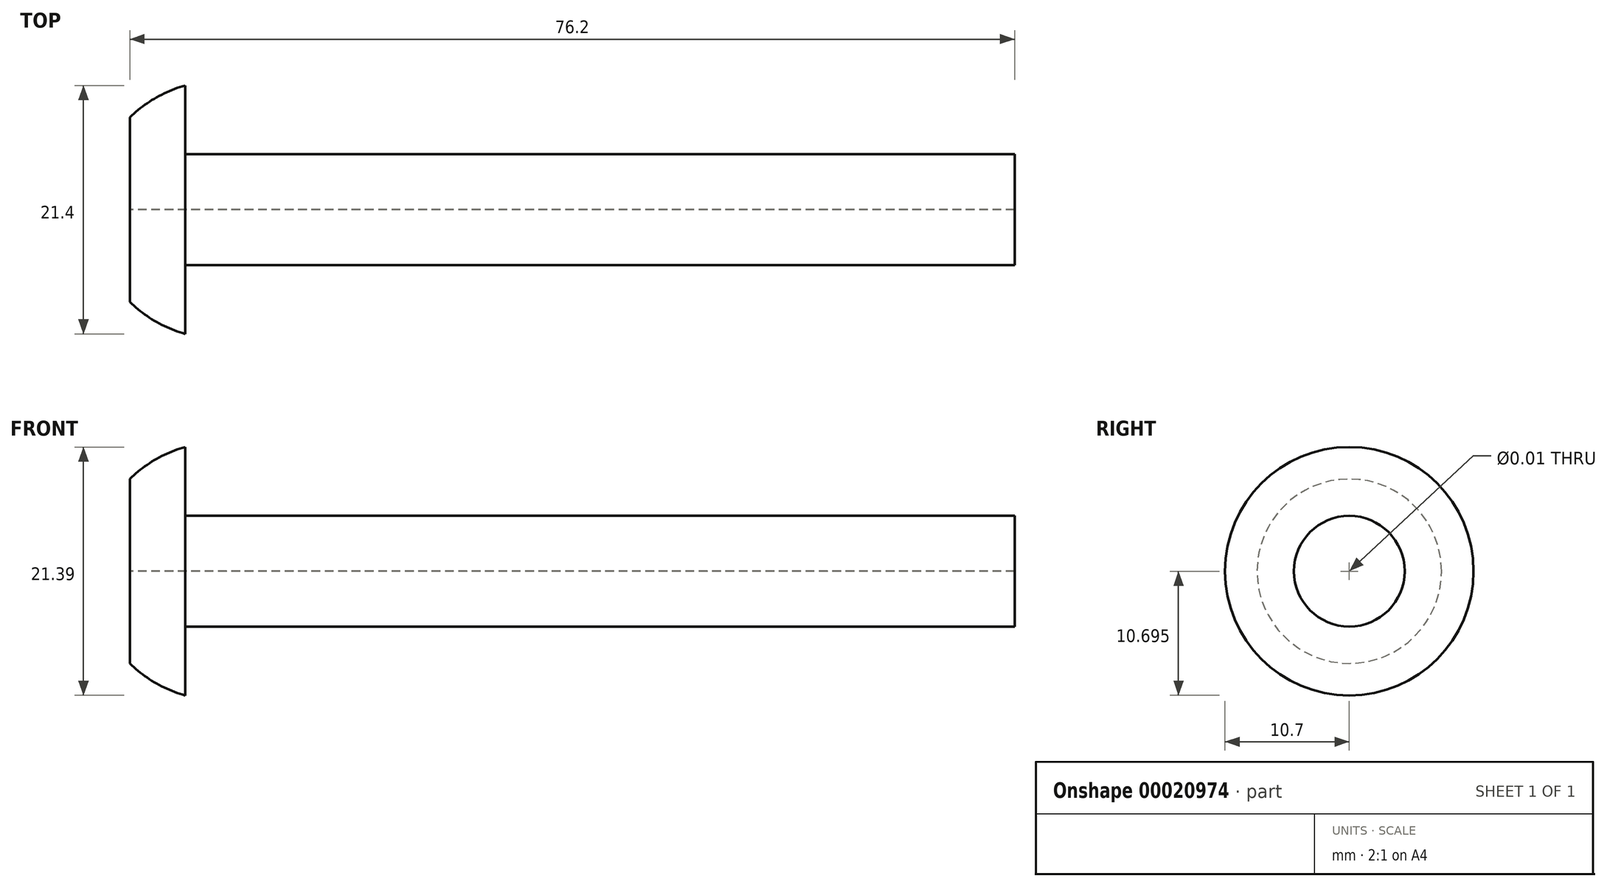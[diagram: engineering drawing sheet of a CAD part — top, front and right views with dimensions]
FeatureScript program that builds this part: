
annotation { "Feature Type Name" : "Feature", "Feature Type Description" : "" }
export const myFeature = defineFeature(function(context is Context, id is Id, definition is map)
    precondition{}
    {
        {
            var Q0;
            Q0=qCreatedBy(makeId("Front.planeOp"),FACE);
            var sketch = newSketch(context, id + "F0", { "sketchPlane" : qUnion([Q0])});
            skPoint(sketch, "E0", {"position": v(31.69, -5.39) * mm});
            skLineSegment(sketch, "E1", {"start": v(40.38, 12.9) * mm, "end": v(40.38, 4.95) * mm});
            skLineSegment(sketch, "E2", {"start": v(40.38, 12.9) * mm, "end": v(43.55, 12.9) * mm});
            skLineSegment(sketch, "E3", {"start": v(43.55, 12.9) * mm, "end": v(45.14, 12.9) * mm});
            skLineSegment(sketch, "E4", {"start": v(43.55, 12.9) * mm, "end": v(43.55, 2.78) * mm});
            skLineSegment(sketch, "E5", {"start": v(45.14, 2.2) * mm, "end": v(45.14, 12.9) * mm});
            skArc(sketch, "E6.trimOffspring", {"start": v(40.38, 4.95) * mm, "mid": v(42.58, 3.28) * mm, "end": v(45.14, 2.2) * mm});
            skLineSegment(sketch, "E7", {"start": v(45.14, 12.9) * mm, "end": v(116.58, 12.9) * mm});
            skLineSegment(sketch, "E8", {"start": v(116.58, 12.9) * mm, "end": v(116.58, 8.13) * mm});
            skLineSegment(sketch, "E9", {"start": v(116.58, 8.13) * mm, "end": v(45.14, 8.13) * mm});
            skPoint(sketch, "E10.orphan", {"position": v(43.55, 23) * mm});
            skPoint(sketch, "E11.orphan", {"position": v(40.38, 20.83) * mm});
            skPoint(sketch, "E12.end.orphan", {"position": v(36.45, -10.16) * mm});
            skPoint(sketch, "E13.end.orphan", {"position": v(36.45, -14.92) * mm});
            skPoint(sketch, "E13.start.orphan", {"position": v(34.86, -14.92) * mm});
            skPoint(sketch, "E14.orphan", {"position": v(31.69, -5.4) * mm});
            skPoint(sketch, "E15.end.orphan", {"position": v(36.45, -5.4) * mm});
            skLineSegment(sketch, "E16", {"start": v(40.38, 12.9) * mm, "end": v(116.58, 12.9) * mm});
            skSolve(sketch);
        }
        {
            var Q0;
            {var subQ2=sQuery(id+"F0.wireOp",EDGE,"E1");Q0=makeQuery(id+"F0.imprint","IMPRINT",FACE,{"disambiguationData":[TD([[makeQuery(id+"F0.imprint","IMPRINT",EDGE,{"derivedFrom":subQ2}),1.0]])]});}
            var Q1;
            {var subQ5=sQuery(id+"F0.wireOp",EDGE,"E3");Q1=makeQuery(id+"F0.imprint","IMPRINT",FACE,{"disambiguationData":[TD([[makeQuery(id+"F0.imprint","IMPRINT",EDGE,{"derivedFrom":subQ5}),-1.0]])]});}
            var Q2;
            {var subQ1=sQuery(id+"F0.wireOp",EDGE,"E7");Q2=makeQuery(id+"F0.imprint","IMPRINT",FACE,{"disambiguationData":[TD([[makeQuery(id+"F0.imprint","IMPRINT",EDGE,{"derivedFrom":subQ1}),-1.0]])]});}
            var Q3;
            Q3=sQuery(id+"F0.wireOp",EDGE,"E16");
            revolve(context, id + "F1", {"entities" : qUnion([Q0, Q1, Q2]), "axis" : qUnion([Q3]), "revolveType" : RevolveType.FULL});
        }
    });
